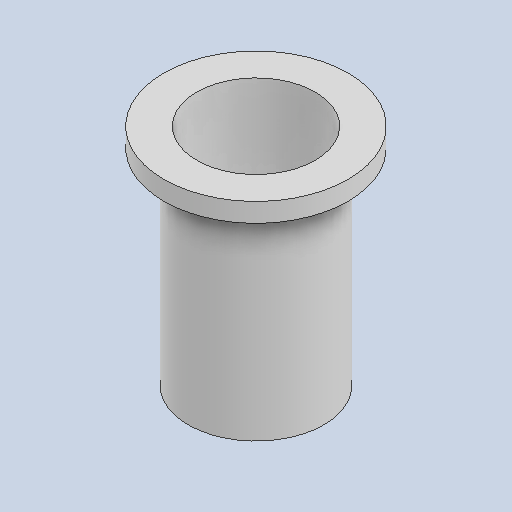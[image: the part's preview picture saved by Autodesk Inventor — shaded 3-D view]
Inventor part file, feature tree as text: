
AUTODESK INVENTOR PART (.ipt)
format: ipt  version: 2022.2 (Build 262287010, 287A)  size: 123,392 bytes
history: native  units: in
note: dims shown in document units (in); Inventor stores cm internally (conversion verified against a paired STEP export)
features: sketch x4, extrude x3, hole x1
ambient origin geometry x8: Origin, YZ Plane, XZ Plane, XY Plane, X Axis, Y Axis, Z Axis, Center Point
bodies: Solid1 (feature_tree)
feature tree (8):
  extrude  "Extrusion1"  Depth=0.07in TaperAngle=0.0deg
  extrude  "Extrusion2"  Depth=0.76in TaperAngle=0.0deg
  hole  "Hole1"  [1 undecoded]
  extrude  "Extrusion3"  [1 undecoded]
  sketch  "Sketch2"  dims[d0=0.68in d1=0.07in d2=0.0in]
  sketch  "Sketch3"  dims[d3=0.5in d4=0.76in d5=0.0in]
  sketch  "Sketch4"  dims[d6=0.3298in d7=0.465in d8=0.375in d9=0.25in d10=0.5635in d11=1.0in d12=0.8108in d13=0.437in]
  sketch  "Sketch5"  dims[d14=0.361in d15=0.0in]
note: 2 required parameter values undecoded (feature->parameter linkage not recoverable at this tier; creation-order binding heuristic only, values carry confidence <= 0.55)
